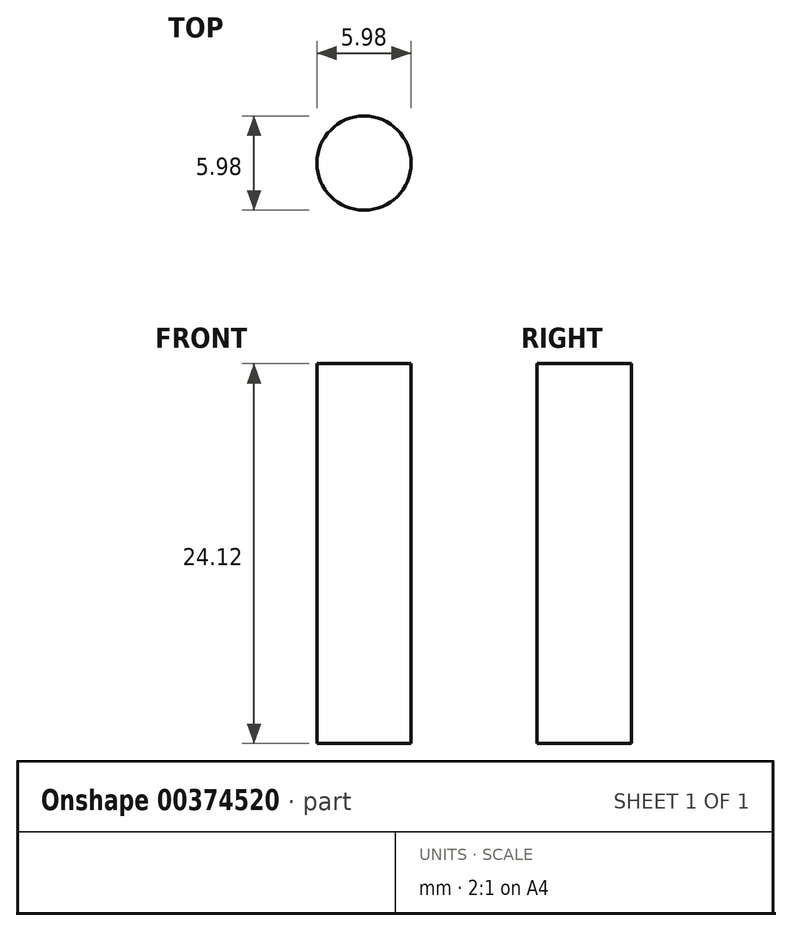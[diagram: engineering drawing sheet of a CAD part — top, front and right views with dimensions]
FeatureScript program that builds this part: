
annotation { "Feature Type Name" : "Feature", "Feature Type Description" : "" }
export const myFeature = defineFeature(function(context is Context, id is Id, definition is map)
    precondition{}
    {
        {
            var Q0;
            Q0=qCreatedBy(makeId("Front.planeOp"),FACE);
            var sketch = newSketch(context, id + "F0", { "sketchPlane" : qUnion([Q0])});
            skLineSegment(sketch, "E0.bottom", {"start": v(-2.99, -12.06) * mm, "end": v(2.99, -12.06) * mm});
            skLineSegment(sketch, "E0.top", {"start": v(-2.99, 12.06) * mm, "end": v(2.99, 12.06) * mm});
            skLineSegment(sketch, "E0.left", {"start": v(-2.99, -12.06) * mm, "end": v(-2.99, 12.06) * mm});
            skLineSegment(sketch, "E0.right", {"start": v(2.99, -12.06) * mm, "end": v(2.99, 12.06) * mm});
            skPoint(sketch, "E0.middle", {"position": v(0, 0) * mm});
            skPoint(sketch, "E1", {"position": v(0, 12.06) * mm});
            skPoint(sketch, "E2", {"position": v(0, -12.06) * mm});
            skLineSegment(sketch, "E3", {"start": v(0, 12.06) * mm, "end": v(0, -12.06) * mm});
            skSolve(sketch);
        }
        {
            var Q0;
            {var subQ0=sQuery(id+"F0.wireOp",EDGE,"E0.left");Q0=makeQuery(id+"F0.imprint","IMPRINT",FACE,{"disambiguationData":[TD([[makeQuery(id+"F0.imprint","IMPRINT",EDGE,{"derivedFrom":subQ0}),-1.0]])]});}
            var Q1;
            Q1=sQuery(id+"F0.wireOp",EDGE,"E3");
            revolve(context, id + "F1", {"entities" : qUnion([Q0]), "axis" : qUnion([Q1]), "revolveType" : RevolveType.FULL});
        }
    });
